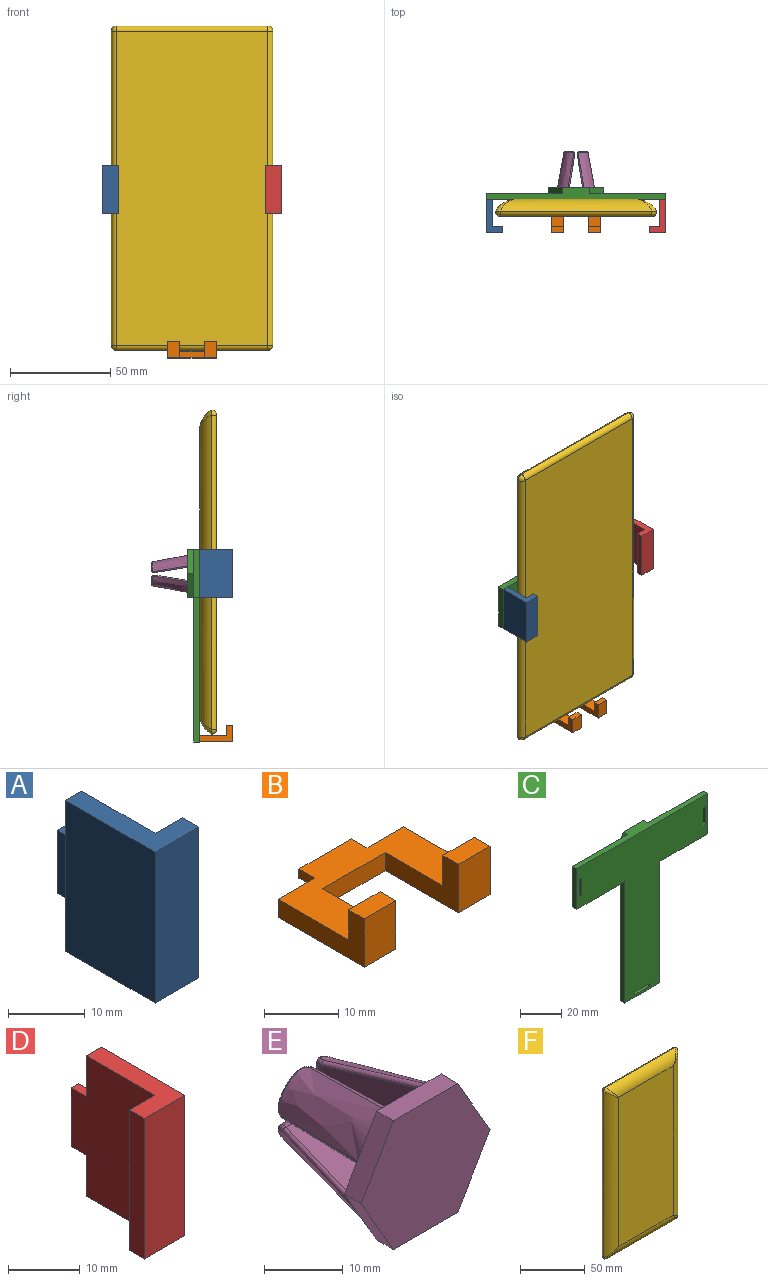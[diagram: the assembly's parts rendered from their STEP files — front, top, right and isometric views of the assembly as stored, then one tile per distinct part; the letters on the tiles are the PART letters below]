
ASSEMBLY  parts=6 mates=5
PART A: 12 faces, bbox 8x19.5x24 mm
  f0: plane 16.5x8mm, normal (0,0,-1), area 64.5mm2, adj f1,f4,f5,f6,f7,f11
  f1: plane 24x16.5mm, normal (1,0,0), area 354mm2, adj f0,f2,f3,f7,f8,f10,f11
  f2: plane 16.5x8mm, normal (0,0,1), area 64.5mm2, adj f1,f4,f5,f6,f7,f11
  f3: plane 10x1.5mm, normal (0,1,0), area 15mm2, adj f1,f8,f9,f10
  f4: plane 24x16.5mm, normal (-1,0,0), area 396mm2, adj f0,f2,f6,f11
  f5: plane 24x3mm, normal (1,0,0), area 72mm2, adj f0,f2,f6,f7
  f6: plane 24x8mm, normal (0,-1,0), area 192mm2, adj f0,f2,f4,f5
  f7: plane 24x5mm, normal (0,1,0), area 120mm2, adj f0,f1,f2,f5
  f8: plane 3x1.5mm, normal (0,0,1), area 4.5mm2, adj f1,f3,f9,f11
  f9: plane 10x3mm, normal (-1,0,0), area 30mm2, adj f3,f8,f10,f11
  f10: plane 3x1.5mm, normal (0,0,-1), area 4.5mm2, adj f1,f3,f9,f11
  f11: plane 24x3mm, normal (0,1,0), area 57mm2, adj f0,f1,f2,f4,f8,f9,f10
PART B: 18 faces, bbox 24x19.5x8 mm
  f0: plane 10x1.5mm, normal (0,1,0), area 15mm2, adj f1,f2,f3,f4
  f1: plane 24x16.5mm, normal (0,0,1), area 222mm2, adj f0,f3,f4,f5,f6,f7,f9,f12
  f2: plane 10x3mm, normal (0,0,-1), area 30mm2, adj f0,f3,f4,f5
  f3: plane 3x1.5mm, normal (-1,0,0), area 4.5mm2, adj f0,f1,f2,f5
  f4: plane 3x1.5mm, normal (1,0,0), area 4.5mm2, adj f0,f1,f2,f5
  f5: plane 24x3mm, normal (0,1,0), area 57mm2, adj f1,f2,f3,f4,f7,f8,f16
  f6: plane 14x8mm, normal (1,0,0), area 57mm2, adj f1,f8,f9,f10,f11,f17
  f7: plane 16.5x8mm, normal (-1,0,0), area 64.5mm2, adj f1,f5,f8,f9,f10,f11
  f8: plane 24x16.5mm, normal (0,0,-1), area 228mm2, adj f5,f6,f7,f11,f12,f15,f16,f17
  f9: plane 6x5mm, normal (0,1,0), area 30mm2, adj f1,f6,f7,f10
  f10: plane 6x3mm, normal (0,0,1), area 18mm2, adj f6,f7,f9,f11
  f11: plane 8x6mm, normal (0,-1,0), area 48mm2, adj f6,f7,f8,f10
  f12: plane 14x8mm, normal (-1,0,0), area 57mm2, adj f1,f8,f13,f14,f15,f17
  f13: plane 6x5mm, normal (0,1,0), area 30mm2, adj f1,f12,f14,f16
  f14: plane 6x3mm, normal (0,0,1), area 18mm2, adj f12,f13,f15,f16
  f15: plane 8x6mm, normal (0,-1,0), area 48mm2, adj f8,f12,f14,f16
  f16: plane 16.5x8mm, normal (1,0,0), area 64.5mm2, adj f1,f5,f8,f13,f14,f15
  f17: plane 12x3mm, normal (0,-1,0), area 36mm2, adj f1,f6,f8,f12
PART C: 35 faces, bbox 89.6x6x96 mm
  f0: plane 72x3mm, normal (-1,0,0), area 216mm2, adj f2,f3,f4,f5
  f1: plane 72x3mm, normal (1,0,0), area 216mm2, adj f2,f3,f4,f9
  f2: plane 24x3mm, normal (0,0,-1), area 72mm2, adj f0,f1,f3,f4
  f3: plane 96x89.6mm, normal (0,1,0), area 3331.1mm2, adj f0,f1,f2,f5,f6,f7,f8,f9
  f4: plane 96x89.6mm, normal (0,-1,0), area 3829.9mm2, adj f0,f1,f2,f5,f6,f7,f8,f9
  f5: plane 32.8x3mm, normal (0,0,-1), area 98.4mm2, adj f0,f3,f4,f8
  f6: plane 24x3mm, normal (1,0,0), area 72mm2, adj f3,f4,f7,f9
  f7: plane 89.6x6mm, normal (0,0,1), area 310.4mm2, adj f3,f4,f6,f8,f16,f17,f21
  f8: plane 24x3mm, normal (-1,0,0), area 72mm2, adj f3,f4,f5,f7
  f9: plane 32.8x3mm, normal (0,0,-1), area 98.4mm2, adj f1,f3,f4,f6
  f10: plane 10.1x5.83mm, normal (0.87,0,-0.5), area 35mm2, adj f11,f20,f21,f22
  f11: plane 10.1x5.83mm, normal (0.87,0,0.5), area 35mm2, adj f10,f12,f21,f22
  f12: plane 11.66x3mm, normal (0,0,1), area 35mm2, adj f11,f13,f21,f22
  f13: plane 10.1x5.83mm, normal (-0.87,0,0.5), area 35mm2, adj f12,f14,f21,f22
  f14: plane 10.1x5.83mm, normal (-0.87,0,-0.5), area 35mm2, adj f13,f20,f21,f22
  f15: plane 12x6.93mm, normal (-0.87,0,-0.5), area 41.6mm2, adj f3,f16,f19,f21
  f16: plane 12x6.93mm, normal (-0.87,0,0.5), area 41.6mm2, adj f3,f7,f15,f21
  f17: plane 12x6.93mm, normal (0.87,0,0.5), area 41.6mm2, adj f3,f7,f18,f21
  f18: plane 12x6.93mm, normal (0.87,0,-0.5), area 41.6mm2, adj f3,f17,f19,f21
  f19: plane 13.86x3mm, normal (0,0,-1), area 41.6mm2, adj f3,f15,f18,f21
  f20: plane 11.66x3mm, normal (0,0,-1), area 35mm2, adj f10,f14,f21,f22
  f21: plane 27.71x24mm, normal (0,1,0), area 145.5mm2, adj f7,f10,f11,f12,f13,f14,f15,f16
  f22: plane 23.33x20.2mm, normal (0,1,0), area 353.4mm2, adj f10,f11,f12,f13,f14,f20
  f23: plane 10.1x3mm, normal (1,0,0), area 30.3mm2, adj f3,f4,f24,f25
  f24: plane 3x1.6mm, normal (0,0,-1), area 4.8mm2, adj f3,f4,f23,f26
  f25: plane 3x1.6mm, normal (0,0,1), area 4.8mm2, adj f3,f4,f23,f26
  f26: plane 10.1x3mm, normal (-1,0,0), area 30.3mm2, adj f3,f4,f24,f25
  f27: plane 10.1x3mm, normal (0,0,1), area 30.3mm2, adj f3,f4,f28,f29
  f28: plane 3x1.6mm, normal (1,0,0), area 4.8mm2, adj f3,f4,f27,f30
  f29: plane 3x1.6mm, normal (-1,0,0), area 4.8mm2, adj f3,f4,f27,f30
  f30: plane 10.1x3mm, normal (0,0,-1), area 30.3mm2, adj f3,f4,f28,f29
  f31: plane 10.1x3mm, normal (1,0,0), area 30.3mm2, adj f3,f4,f32,f33
  f32: plane 3x1.6mm, normal (0,0,-1), area 4.8mm2, adj f3,f4,f31,f34
  f33: plane 3x1.6mm, normal (0,0,1), area 4.8mm2, adj f3,f4,f31,f34
  f34: plane 10.1x3mm, normal (-1,0,0), area 30.3mm2, adj f3,f4,f32,f33
PART D: 12 faces, bbox 8x19.5x24 mm
  f0: plane 16.5x8mm, normal (0,0,-1), area 64.5mm2, adj f1,f3,f5,f6,f7,f11
  f1: plane 24x16.5mm, normal (1,0,0), area 396mm2, adj f0,f4,f6,f11
  f2: plane 10x1.5mm, normal (0,1,0), area 15mm2, adj f3,f8,f9,f10
  f3: plane 24x16.5mm, normal (-1,0,0), area 354mm2, adj f0,f2,f4,f7,f8,f10,f11
  f4: plane 16.5x8mm, normal (0,0,1), area 64.5mm2, adj f1,f3,f5,f6,f7,f11
  f5: plane 24x3mm, normal (-1,0,0), area 72mm2, adj f0,f4,f6,f7
  f6: plane 24x8mm, normal (0,-1,0), area 192mm2, adj f0,f1,f4,f5
  f7: plane 24x5mm, normal (0,1,0), area 120mm2, adj f0,f3,f4,f5
  f8: plane 3x1.5mm, normal (0,0,-1), area 4.5mm2, adj f2,f3,f9,f11
  f9: plane 10x3mm, normal (1,0,0), area 30mm2, adj f2,f8,f10,f11
  f10: plane 3x1.5mm, normal (0,0,1), area 4.5mm2, adj f2,f3,f9,f11
  f11: plane 24x3mm, normal (0,1,0), area 57mm2, adj f0,f1,f3,f4,f8,f9,f10
PART E: 60 faces, bbox 23.2x22.7x20.1 mm
  f0: bspline ~17.61x8.2mm, area 134.1mm2, adj f4,f18,f19,f20,f48,f52
  f1: bspline ~17.61x8.2mm, area 134.1mm2, adj f4,f22,f23,f24,f43,f47
  f2: bspline ~17.61x8.2mm, area 134.1mm2, adj f4,f26,f27,f28,f38,f42
  f3: bspline ~17.61x8.2mm, area 134.1mm2, adj f4,f30,f31,f32,f33,f37
  f4: plane 23.16x20.06mm, normal (0,1,0), area 246.6mm2, adj f0,f1,f2,f3,f6,f7,f9,f10
  f5: plane 3.08x3.08mm, normal (0,1,0), area 6mm2, adj f31,f34,f36
  f6: plane 16.26x7.57mm, normal (-0.99,-0.16,0), area 78.7mm2, adj f4,f29,f32,f34
  f7: plane 16.26x7.57mm, normal (0,-0.16,-0.99), area 78.7mm2, adj f4,f29,f30,f36
  f8: plane 3.08x3.08mm, normal (0,1,0), area 6mm2, adj f27,f39,f41
  f9: plane 16.26x7.57mm, normal (0.99,-0.16,0), area 78.7mm2, adj f4,f25,f28,f39
  f10: plane 16.26x7.57mm, normal (0,-0.16,-0.99), area 78.7mm2, adj f4,f25,f26,f41
  f11: plane 3.08x3.08mm, normal (0,1,0), area 6mm2, adj f23,f44,f46
  f12: plane 16.26x7.57mm, normal (-0.99,-0.16,0), area 78.7mm2, adj f4,f21,f24,f44
  f13: plane 16.26x7.57mm, normal (0,-0.16,0.99), area 78.7mm2, adj f4,f21,f22,f46
  f14: plane 3.08x3.08mm, normal (0,1,0), area 6mm2, adj f19,f49,f51
  f15: plane 16.26x7.57mm, normal (0,-0.16,0.99), area 78.7mm2, adj f4,f17,f20,f49
  f16: plane 16.26x7.57mm, normal (0.99,-0.16,0), area 78.7mm2, adj f4,f17,f18,f51
  f17: cylinder r=0.5mm len=16.29mm, axis (-0.16,-0.98,-0.16), area 12.9mm2, adj f4,f15,f16,f50
  f18: bspline ~21.24x4.63mm, area 15.9mm2, adj f0,f4,f16,f52
  f19: bspline ~4.81x4.71mm, area 3.2mm2, adj f0,f14,f48,f52
  f20: bspline ~21.24x4.63mm, area 15.9mm2, adj f0,f4,f15,f48
  f21: cylinder r=0.5mm len=16.29mm, axis (0.16,-0.98,-0.16), area 12.9mm2, adj f4,f12,f13,f45
  f22: bspline ~21.24x4.63mm, area 15.9mm2, adj f1,f4,f13,f47
  f23: bspline ~4.81x4.71mm, area 3.2mm2, adj f1,f11,f43,f47
  f24: bspline ~21.24x4.63mm, area 15.9mm2, adj f1,f4,f12,f43
  f25: cylinder r=0.5mm len=16.29mm, axis (-0.16,-0.98,0.16), area 12.9mm2, adj f4,f9,f10,f40
  f26: bspline ~21.24x4.63mm, area 15.9mm2, adj f2,f4,f10,f42
  f27: bspline ~4.81x4.71mm, area 3.2mm2, adj f2,f8,f38,f42
  f28: bspline ~21.24x4.63mm, area 15.9mm2, adj f2,f4,f9,f38
  f29: cylinder r=0.5mm len=16.29mm, axis (-0.16,0.98,-0.16), area 12.9mm2, adj f4,f6,f7,f35
  f30: bspline ~19.91x4.39mm, area 15.9mm2, adj f3,f4,f7,f37
  f31: bspline ~4.58x4.36mm, area 3.2mm2, adj f3,f5,f33,f37
  f32: bspline ~19.91x4.39mm, area 15.9mm2, adj f3,f4,f6,f33
  f33: bspline ~1.99x1.88mm, area 1.9mm2, adj f3,f31,f32,f34
  f34: cylinder r=1.5mm len=4.6mm, axis (0,0,-1), area 10mm2, adj f5,f6,f33,f35
  f35: bspline ~1.94x1.5mm, area 0.9mm2, adj f29,f34,f36
  f36: cylinder r=1.5mm len=4.6mm, axis (-1,0,0), area 10mm2, adj f5,f7,f35,f37
  f37: bspline ~2.06x1.83mm, area 1.9mm2, adj f3,f30,f31,f36
  f38: bspline ~2.06x1.83mm, area 1.9mm2, adj f2,f27,f28,f39
  f39: cylinder r=1.5mm len=4.6mm, axis (0,0,-1), area 10mm2, adj f8,f9,f38,f40
  f40: bspline ~1.94x1.5mm, area 0.9mm2, adj f25,f39,f41
  f41: cylinder r=1.5mm len=4.6mm, axis (1,0,0), area 10mm2, adj f8,f10,f40,f42
  f42: bspline ~1.99x1.88mm, area 1.9mm2, adj f2,f26,f27,f41
  f43: bspline ~2.06x1.83mm, area 1.9mm2, adj f1,f23,f24,f44
  f44: cylinder r=1.5mm len=4.6mm, axis (0,0,1), area 10mm2, adj f11,f12,f43,f45
  f45: bspline ~1.94x1.5mm, area 0.9mm2, adj f21,f44,f46
  f46: cylinder r=1.5mm len=4.6mm, axis (-1,0,0), area 10mm2, adj f11,f13,f45,f47
  f47: bspline ~1.99x1.88mm, area 1.9mm2, adj f1,f22,f23,f46
  f48: bspline ~2.06x1.83mm, area 1.9mm2, adj f0,f19,f20,f49
  f49: cylinder r=1.5mm len=4.6mm, axis (1,0,0), area 10mm2, adj f14,f15,f48,f50
  f50: bspline ~1.94x1.5mm, area 0.9mm2, adj f17,f49,f51
  f51: cylinder r=1.5mm len=4.6mm, axis (0,0,1), area 10mm2, adj f14,f16,f50,f52
  f52: bspline ~1.99x1.88mm, area 1.9mm2, adj f0,f18,f19,f51
  f53: plane 11.55x3mm, normal (0,0,1), area 34.6mm2, adj f4,f54,f58,f59
  f54: plane 10x5.77mm, normal (0.87,0,0.5), area 34.6mm2, adj f4,f53,f55,f59
  f55: plane 10x5.77mm, normal (0.87,0,-0.5), area 34.6mm2, adj f4,f54,f56,f59
  f56: plane 11.55x3mm, normal (0,0,-1), area 34.6mm2, adj f4,f55,f57,f59
  f57: plane 10x5.77mm, normal (-0.87,0,-0.5), area 34.6mm2, adj f4,f56,f58,f59
  f58: plane 10x5.77mm, normal (-0.87,0,0.5), area 34.6mm2, adj f4,f53,f57,f59
  f59: plane 23.09x20mm, normal (0,-1,0), area 346.4mm2, adj f53,f54,f55,f56,f57,f58
PART F: 18 faces, bbox 80.6x8.5x162 mm
  f0: plane 141.22x59.82mm, normal (0,-1,0), area 8446.9mm2, adj f10,f13,f14,f17
  f1: plane 157x75.6mm, normal (0,1,0), area 11869.2mm2, adj f3,f4,f7,f8
  f2: sphere r=2.5mm, area 9.8mm2, adj f3,f4,f11
  f3: cylinder r=2.5mm len=75.6mm, axis (-1,0,0), area 296.9mm2, adj f1,f2,f5,f13
  f4: cylinder r=2.5mm len=157mm, axis (0,0,-1), area 616.5mm2, adj f1,f2,f6,f10
  f5: sphere r=2.5mm, area 13.4mm2, adj f3,f7,f15
  f6: sphere r=2.5mm, area 9.8mm2, adj f4,f8,f12
  f7: cylinder r=2.5mm len=157mm, axis (0,0,1), area 616.5mm2, adj f1,f5,f9,f17
  f8: cylinder r=2.5mm len=75.6mm, axis (1,0,0), area 296.9mm2, adj f1,f6,f9,f14
  f9: sphere r=2.5mm, area 6.2mm2, adj f7,f8,f16
  f10: cylinder r=12mm len=157mm, axis (0,0,-1), area 1873.7mm2, adj f0,f4,f11,f12
  f11: bspline ~10.39x10.39mm, area 20mm2, adj f2,f10,f13
  f12: bspline ~10.39x10.39mm, area 20mm2, adj f6,f10,f14
  f13: cylinder r=12mm len=75.6mm, axis (1,0,0), area 850.8mm2, adj f0,f3,f11,f15
  f14: cylinder r=12mm len=75.6mm, axis (1,0,0), area 850.8mm2, adj f0,f8,f12,f16
  f15: bspline ~10.39x10.39mm, area 20mm2, adj f5,f13,f17
  f16: bspline ~10.39x10.39mm, area 20mm2, adj f9,f14,f17
  f17: cylinder r=12mm len=157mm, axis (0,0,-1), area 1873.7mm2, adj f0,f7,f15,f16
PLACE A t=(-81.2,-40.39,27.55)mm
PLACE B t=(-94.2,-40.39,40.65)mm
PLACE C t=(-94.2,-40.39,27.55)mm
PLACE D t=(-107.2,-40.39,27.55)mm
PLACE E t=(-94.2,-57.39,27.55)mm
PLACE F rot(axis=(1,0,0),180deg) t=(-237.27,-68.89,1.55)mm
MATE fastened B.f0 <-> C.f3  axis (0,1,0) through (-94.2,-57.39,-53.35)mm
MATE fastened E.f59 <-> C.f22  axis (0,-1,0) through (-94.2,-57.39,27.55)mm
MATE planar C.f4 <-> F.f0  axis (0,-1,0) through (-94.2,-60.39,6.24)mm
MATE fastened D.f2 <-> C.f3  axis (0,1,0) through (-50.9,-57.39,27.55)mm
MATE fastened A.f3 <-> C.f3  axis (0,1,0) through (-137.5,-57.39,27.55)mm
